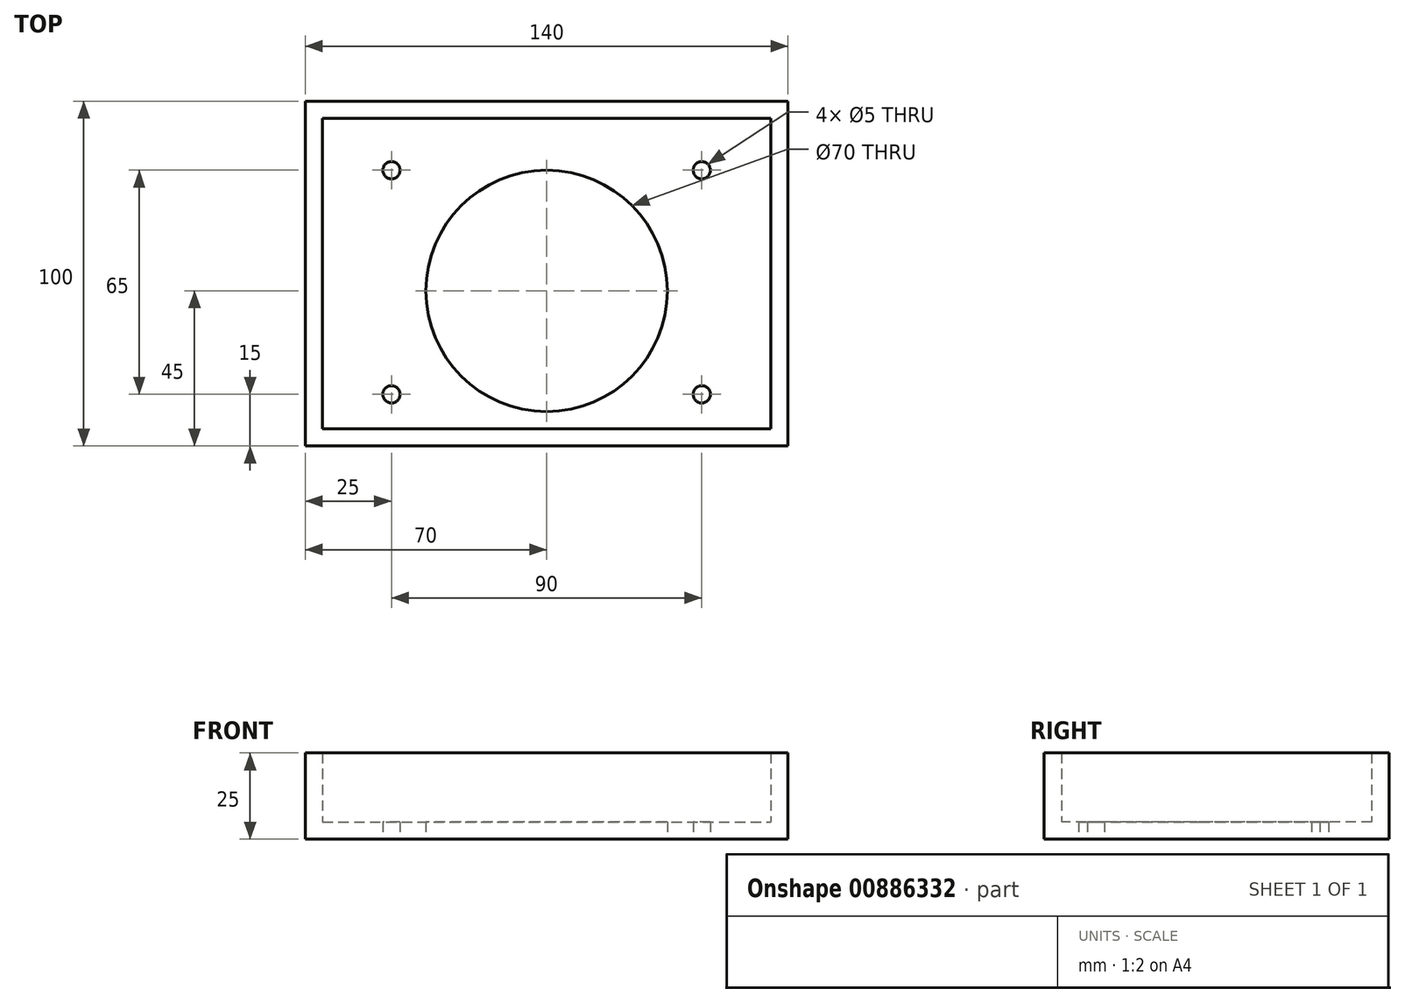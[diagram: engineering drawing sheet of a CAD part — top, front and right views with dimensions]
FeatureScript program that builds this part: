
annotation { "Feature Type Name" : "Feature", "Feature Type Description" : "" }
export const myFeature = defineFeature(function(context is Context, id is Id, definition is map)
    precondition{}
    {
        {
            var Q0;
            Q0=qCreatedBy(makeId("Top.planeOp"),FACE);
            var sketch = newSketch(context, id + "F0", { "sketchPlane" : qUnion([Q0])});
            skLineSegment(sketch, "E0.bottom", {"start": v(0, 0) * mm, "end": v(140, 0) * mm});
            skLineSegment(sketch, "E0.top", {"start": v(0, 100) * mm, "end": v(140, 100) * mm});
            skLineSegment(sketch, "E0.left", {"start": v(0, 0) * mm, "end": v(0, 100) * mm});
            skLineSegment(sketch, "E0.right", {"start": v(140, 0) * mm, "end": v(140, 100) * mm});
            skCircle(sketch, "E1", {"center": v(25, 15) * mm, "radius": 2.5 * mm});
            skCircle(sketch, "E2.0.1.0", {"center": v(25, 80) * mm, "radius": 2.5 * mm});
            skCircle(sketch, "E2.1.0.0", {"center": v(115, 15) * mm, "radius": 2.5 * mm});
            skCircle(sketch, "E2.1.1.0", {"center": v(115, 80) * mm, "radius": 2.5 * mm});
            skLineSegment(sketch, "E2.direction1", {"start": v(25, 15) * mm, "end": v(115, 15) * mm, "construction": true});
            skLineSegment(sketch, "E2.direction2", {"start": v(25, 15) * mm, "end": v(25, 80) * mm, "construction": true});
            skCircle(sketch, "E3", {"center": v(70, 45) * mm, "radius": 35 * mm});
            skLineSegment(sketch, "E4.bottom", {"start": v(5, 95) * mm, "end": v(135, 95) * mm});
            skLineSegment(sketch, "E4.top", {"start": v(5, 5) * mm, "end": v(135, 5) * mm});
            skLineSegment(sketch, "E4.left", {"start": v(5, 95) * mm, "end": v(5, 5) * mm});
            skLineSegment(sketch, "E4.right", {"start": v(135, 95) * mm, "end": v(135, 5) * mm});
            skSolve(sketch);
        }
        {
            var Q0;
            Q0=makeQuery(id+"F0.imprint","IMPRINT",FACE,{"disambiguationData":[TD([[makeQuery(id+"F0.imprint","IMPRINT",EDGE,{"derivedFrom":sQuery(id+"F0.wireOp",EDGE,"E0.bottom")}),1.0]])]});
            extrude(context, id + "F1", {"entities" : qUnion([Q0]), "depth" : 25 * mm, "offsetDistance" : 25 * mm});
        }
        {
            var Q0;
            Q0=makeQuery(id+"F0.imprint","IMPRINT",FACE,{"disambiguationData":[TD([[makeQuery(id+"F0.imprint","IMPRINT",EDGE,{"derivedFrom":sQuery(id+"F0.wireOp",EDGE,"E1")}),-1.0]])]});
            extrude(context, id + "F2", {"entities" : qUnion([Q0]), "operationType" : NewBodyOperationType.ADD, "depth" : 5 * mm, "offsetDistance" : 25 * mm});
        }
    });
